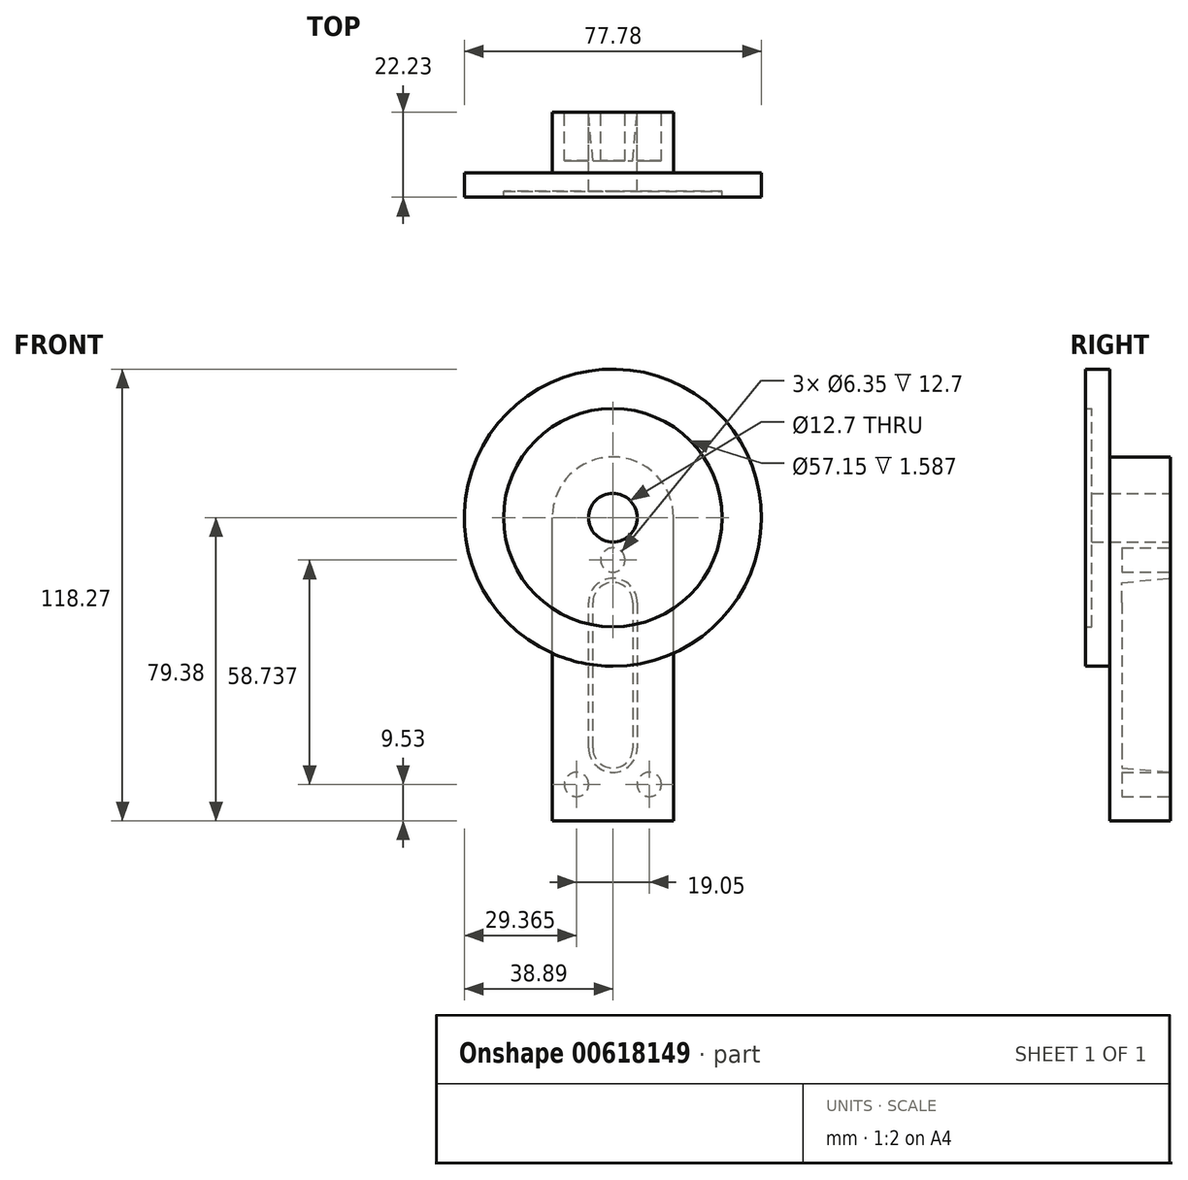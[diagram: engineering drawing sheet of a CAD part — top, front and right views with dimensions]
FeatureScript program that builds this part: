
annotation { "Feature Type Name" : "Feature", "Feature Type Description" : "" }
export const myFeature = defineFeature(function(context is Context, id is Id, definition is map)
    precondition{}
    {
        {
            var Q0;
            Q0=qCreatedBy(makeId("Front.planeOp"),FACE);
            var sketch = newSketch(context, id + "F0", { "sketchPlane" : qUnion([Q0])});
            skCircle(sketch, "E0", {"center": v(0, 0) * mm, "radius": 38.9 * mm});
            skCircle(sketch, "E1", {"center": v(0, 0) * mm, "radius": 6.35 * mm});
            skSolve(sketch);
        }
        {
            var Q0;
            Q0=qSketchRegion(id+"F0",true);
            extrude(context, id + "F1", {"entities" : qUnion([Q0]), "depth" : 4.76 * mm});
        }
        {
            var Q0;
            Q0=makeQuery(id+"F1.opExtrude","CAP_FACE",FACE,{"disambiguationData":[OSD([sQuery(id+"F0.wireOp",EDGE,"E0"),sQuery(id+"F0.wireOp",EDGE,"E1")])],"isStart":false});
            var sketch = newSketch(context, id + "F2", { "sketchPlane" : qUnion([Q0])});
            skCircle(sketch, "E2", {"center": v(0, 0) * mm, "radius": 28.58 * mm});
            skCircle(sketch, "E3.0.0", {"center": v(0, 0) * mm, "radius": 38.9 * mm});
            skSolve(sketch);
        }
        {
            var Q0;
            Q0=qSketchRegion(id+"F2",true);
            extrude(context, id + "F3", {"entities" : qUnion([Q0]), "operationType" : NewBodyOperationType.ADD, "depth" : 1.59 * mm});
        }
        {
            var Q0;
            Q0=makeQuery(id+"F1.opExtrude","CAP_FACE",FACE,{"disambiguationData":[OSD([sQuery(id+"F0.wireOp",EDGE,"E0"),sQuery(id+"F0.wireOp",EDGE,"E1")])],"isStart":true});
            var sketch = newSketch(context, id + "F4", { "sketchPlane" : qUnion([Q0])});
            skLineSegment(sketch, "E4.bottom", {"start": v(15.88, -79.38) * mm, "end": v(-15.87, -79.38) * mm});
            skLineSegment(sketch, "E4.top", {"start": v(15.87, 79.37) * mm, "end": v(-15.88, 79.37) * mm});
            skLineSegment(sketch, "E4.left", {"start": v(15.88, -79.38) * mm, "end": v(15.88, 79.37) * mm});
            skLineSegment(sketch, "E4.right", {"start": v(-15.88, -79.38) * mm, "end": v(-15.88, 79.37) * mm});
            skPoint(sketch, "E4.middle", {"position": v(0, 0) * mm});
            skCircle(sketch, "E5", {"center": v(0, 0) * mm, "radius": 15.88 * mm});
            skSolve(sketch);
        }
        {
            var Q0;
            {var subQ0=sQuery(id+"F4.wireOp",EDGE,"E4.bottom");Q0=makeQuery(id+"F4.imprint","IMPRINT",FACE,{"disambiguationData":[TD([[makeQuery(id+"F4.imprint","IMPRINT",EDGE,{"derivedFrom":subQ0}),-1.0]])]});}
            var Q1;
            {var subQ0=sQuery(id+"F4.wireOp",EDGE,"E5");var subQ1=sQuery(id+"F4.wireOp",EDGE,"E4.left");var subQ2=makeQuery(id+"F4.imprint","INTERSECT",VERTEX,{"derivedFrom":[subQ1,subQ0]});Q1=makeQuery(id+"F4.imprint","IMPRINT",FACE,{"disambiguationData":[TD([[makeQuery(id+"F4.imprint","IMPRINT",EDGE,{"disambiguationData":[TD([[subQ2,1.0]])],"derivedFrom":subQ1}),1.0]])]});}
            var Q2;
            Q2=makeQuery(id+"F4.imprint","IMPRINT",FACE,{"disambiguationData":[TD([[makeQuery(id+"F4.imprint","IMPRINT",EDGE,{"derivedFrom":makeQuery(id+"F1.opExtrude","CAP_EDGE",EDGE,{"disambiguationData":[OSD([sQuery(id+"F0.wireOp",EDGE,"E1")])],"isStart":true})}),1.0]])]});
            extrude(context, id + "F5", {"entities" : qUnion([Q0, Q1, Q2]), "operationType" : NewBodyOperationType.ADD, "depth" : 15.88 * mm});
        }
        {
            var Q0;
            Q0=makeQuery(id+"F5.opExtrude","CAP_FACE",FACE,{"disambiguationData":[OSD([sQuery(id+"F0.wireOp",EDGE,"E1"),sQuery(id+"F4.wireOp",EDGE,"E4.bottom"),sQuery(id+"F4.wireOp",EDGE,"E4.left"),sQuery(id+"F4.wireOp",EDGE,"E4.right"),sQuery(id+"F4.wireOp",EDGE,"E5")])],"isStart":false});
            var sketch = newSketch(context, id + "F6", { "sketchPlane" : qUnion([Q0])});
            skLineSegment(sketch, "E6", {"start": v(0, -79.38) * mm, "end": v(0, 0) * mm});
            skLineSegment(sketch, "E7.bottom", {"start": v(6.35, -60.33) * mm, "end": v(-6.35, -60.33) * mm});
            skLineSegment(sketch, "E7.top", {"start": v(6.35, -22.23) * mm, "end": v(-6.35, -22.23) * mm});
            skLineSegment(sketch, "E7.left", {"start": v(6.35, -60.33) * mm, "end": v(6.35, -22.23) * mm});
            skLineSegment(sketch, "E7.right", {"start": v(-6.35, -60.33) * mm, "end": v(-6.35, -22.23) * mm});
            skPoint(sketch, "E7.middle", {"position": v(0, -41.28) * mm});
            skCircle(sketch, "E8", {"center": v(0, -22.23) * mm, "radius": 6.35 * mm});
            skCircle(sketch, "E9", {"center": v(0, -60.33) * mm, "radius": 6.35 * mm});
            skSolve(sketch);
        }
        {
            var Q0;
            Q0=qSketchRegion(id+"F6",true);
            extrude(context, id + "F7", {"entities" : qUnion([Q0]), "operationType" : NewBodyOperationType.REMOVE, "oppositeDirection" : true, "depth" : 12.7 * mm, "hasDraft" : true, "draftAngle" : 5 * degree, "draftPullDirection" : true});
        }
        {
            var Q0;
            Q0=makeQuery(id+"F5.opExtrude","CAP_FACE",FACE,{"disambiguationData":[OSD([sQuery(id+"F0.wireOp",EDGE,"E1"),sQuery(id+"F4.wireOp",EDGE,"E4.bottom"),sQuery(id+"F4.wireOp",EDGE,"E4.left"),sQuery(id+"F4.wireOp",EDGE,"E4.right"),sQuery(id+"F4.wireOp",EDGE,"E5")])],"isStart":false});
            var sketch = newSketch(context, id + "F8", { "sketchPlane" : qUnion([Q0])});
            skLineSegment(sketch, "E10", {"start": v(0, 0) * mm, "end": v(0, -69.85) * mm});
            skLineSegment(sketch, "E11", {"start": v(9.53, -69.85) * mm, "end": v(-9.52, -69.85) * mm});
            skCircle(sketch, "E12", {"center": v(0, -11.11) * mm, "radius": 3.18 * mm});
            skCircle(sketch, "E13", {"center": v(-9.52, -69.85) * mm, "radius": 3.18 * mm});
            skCircle(sketch, "E14", {"center": v(9.53, -69.85) * mm, "radius": 3.18 * mm});
            skSolve(sketch);
        }
        {
            var Q0;
            Q0=qSketchRegion(id+"F8",true);
            extrude(context, id + "F9", {"entities" : qUnion([Q0]), "operationType" : NewBodyOperationType.REMOVE, "oppositeDirection" : true, "depth" : 12.7 * mm});
        }
    });
